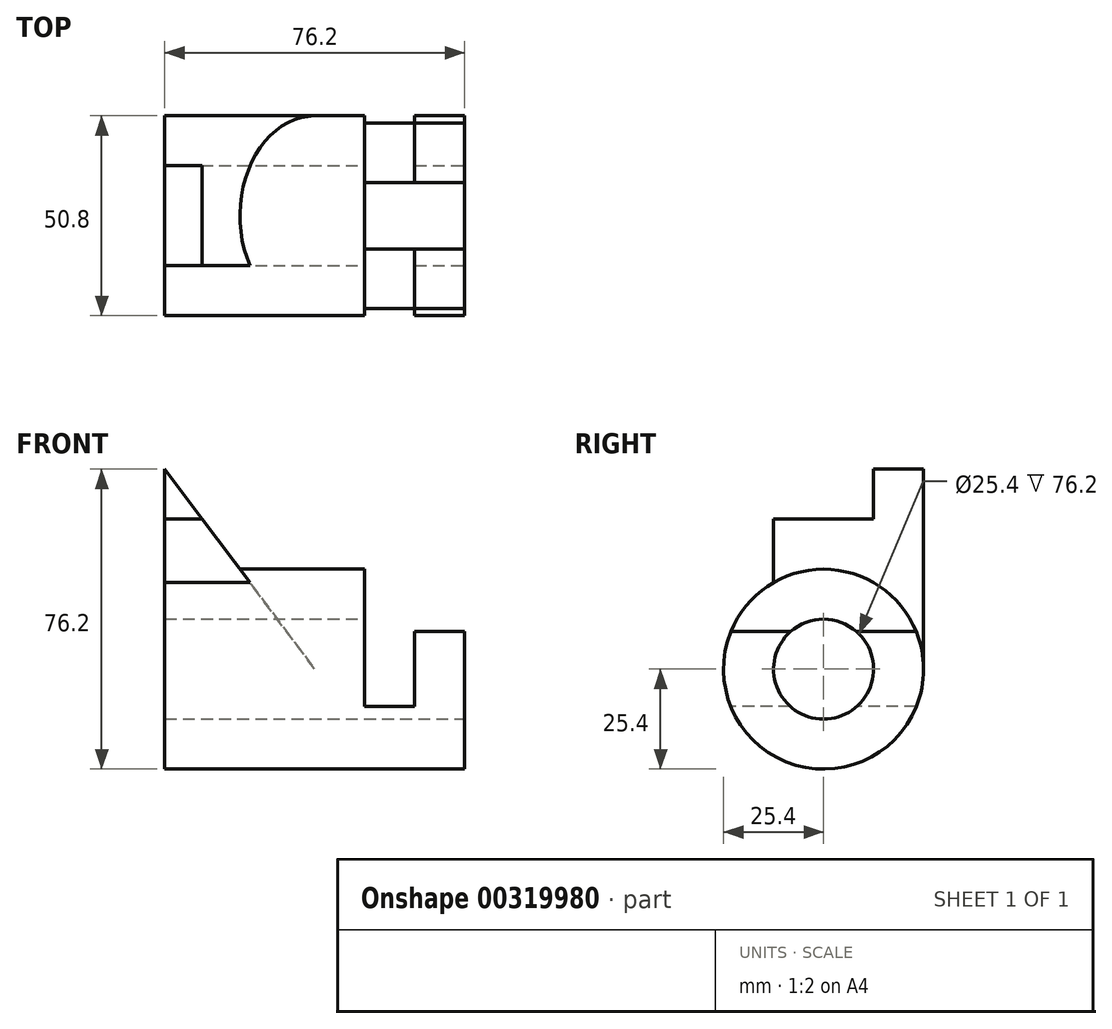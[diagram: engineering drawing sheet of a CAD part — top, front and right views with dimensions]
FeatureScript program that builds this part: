
annotation { "Feature Type Name" : "Feature", "Feature Type Description" : "" }
export const myFeature = defineFeature(function(context is Context, id is Id, definition is map)
    precondition{}
    {
        {
            var Q0;
            Q0=qCreatedBy(makeId("Right.planeOp"),FACE);
            var sketch = newSketch(context, id + "F0", { "sketchPlane" : qUnion([Q0])});
            skCircle(sketch, "E0", {"center": v(0, 0) * mm, "radius": 12.7 * mm});
            skCircle(sketch, "E1", {"center": v(0, 0) * mm, "radius": 25.4 * mm});
            skLineSegment(sketch, "E2", {"start": v(25.4, 0) * mm, "end": v(25.4, 50.8) * mm});
            skLineSegment(sketch, "E3", {"start": v(25.4, 50.8) * mm, "end": v(12.7, 50.8) * mm});
            skLineSegment(sketch, "E4", {"start": v(12.7, 50.8) * mm, "end": v(12.7, 38.1) * mm});
            skLineSegment(sketch, "E5", {"start": v(12.7, 38.1) * mm, "end": v(-12.7, 38.1) * mm});
            skLineSegment(sketch, "E6", {"start": v(-12.7, 38.1) * mm, "end": v(-12.7, 22) * mm});
            skSolve(sketch);
        }
        {
            var Q0;
            Q0 = qSketchRegion(id + "F0", true);
            extrude(context, id + "F1", {"entities" : qUnion([Q0]), "oppositeDirection" : true, "depth" : 76.2 * mm});
        }
        {
            var Q0;
            Q0=makeQuery(id+"F1.opExtrude","CAP_FACE",FACE,{"disambiguationData":[OSD([sQuery(id+"F0.wireOp",EDGE,"E0"),sQuery(id+"F0.wireOp",EDGE,"E1"),sQuery(id+"F0.wireOp",EDGE,"E2"),sQuery(id+"F0.wireOp",EDGE,"E3"),sQuery(id+"F0.wireOp",EDGE,"E4"),sQuery(id+"F0.wireOp",EDGE,"E5"),sQuery(id+"F0.wireOp",EDGE,"E6")])],"isStart":true});
            var sketch = newSketch(context, id + "F2", { "sketchPlane" : qUnion([Q0])});
            skLineSegment(sketch, "E7", {"start": v(25.4, 50.8) * mm, "end": v(-28.4, 50.8) * mm});
            skLineSegment(sketch, "E8", {"start": v(-28.4, 50.8) * mm, "end": v(-28.4, 9.52) * mm});
            skLineSegment(sketch, "E9", {"start": v(-28.4, 9.52) * mm, "end": v(25.4, 9.52) * mm});
            skLineSegment(sketch, "E10", {"start": v(25.4, 9.52) * mm, "end": v(25.4, 50.8) * mm});
            skSolve(sketch);
        }
        {
            var Q0;
            Q0 = qSketchRegion(id + "F2", true);
            extrude(context, id + "F3", {"entities" : qUnion([Q0]), "operationType" : NewBodyOperationType.REMOVE, "oppositeDirection" : true, "depth" : 25.4 * mm});
        }
        {
            var Q0;
            Q0=qCreatedBy(makeId("Front.planeOp"),FACE);
            var sketch = newSketch(context, id + "F4", { "sketchPlane" : qUnion([Q0])});
            skLineSegment(sketch, "E11.bottom", {"start": v(-25.4, 50.8) * mm, "end": v(-12.7, 50.8) * mm});
            skLineSegment(sketch, "E11.top", {"start": v(-25.4, -9.52) * mm, "end": v(-12.7, -9.52) * mm});
            skLineSegment(sketch, "E11.left", {"start": v(-25.4, 50.8) * mm, "end": v(-25.4, -9.52) * mm});
            skLineSegment(sketch, "E11.right", {"start": v(-12.7, 50.8) * mm, "end": v(-12.7, -9.52) * mm});
            skSolve(sketch);
        }
        {
            var Q0;
            Q0 = qSketchRegion(id + "F4", true);
            extrude(context, id + "F5", {"entities" : qUnion([Q0]), "operationType" : NewBodyOperationType.REMOVE, "endBound" : BoundingType.SYMMETRIC, "oppositeDirection" : true, "depth" : 254 * mm});
        }
        {
            var Q0;
            Q0=qCreatedBy(makeId("Front.planeOp"),FACE);
            var sketch = newSketch(context, id + "F6", { "sketchPlane" : qUnion([Q0])});
            skLineSegment(sketch, "E12", {"start": v(-76.2, 50.8) * mm, "end": v(-38.1, 0) * mm});
            skLineSegment(sketch, "E13", {"start": v(-38.1, 0) * mm, "end": v(-76.2, 0) * mm});
            skLineSegment(sketch, "E14", {"start": v(-76.2, 0) * mm, "end": v(-76.2, 50.8) * mm});
            skLineSegment(sketch, "E15", {"start": v(-76.2, 50.8) * mm, "end": v(-38.1, 50.8) * mm});
            skLineSegment(sketch, "E16", {"start": v(-38.1, 50.8) * mm, "end": v(-38.1, 0) * mm});
            skSolve(sketch);
        }
        {
            var Q0;
            Q0=makeQuery(id+"F6.imprint","IMPRINT",FACE,{"disambiguationData":[TD([[makeQuery(id+"F6.imprint","IMPRINT",EDGE,{"derivedFrom":sQuery(id+"F6.wireOp",EDGE,"E12")}),1.0]])]});
            extrude(context, id + "F7", {"entities" : qUnion([Q0]), "operationType" : NewBodyOperationType.REMOVE, "endBound" : BoundingType.THROUGH_ALL, "oppositeDirection" : true, "depth" : 25.4 * mm});
        }
        {
            var Q0;
            Q0=qCreatedBy(makeId("Front.planeOp"),FACE);
            var sketch = newSketch(context, id + "F8", { "sketchPlane" : qUnion([Q0])});
            skLineSegment(sketch, "E17.bottom", {"start": v(-38.1, 50.8) * mm, "end": v(-25.4, 50.8) * mm});
            skLineSegment(sketch, "E17.top", {"start": v(-38.1, 22) * mm, "end": v(-25.4, 22) * mm});
            skLineSegment(sketch, "E17.left", {"start": v(-38.1, 50.8) * mm, "end": v(-38.1, 22) * mm});
            skLineSegment(sketch, "E17.right", {"start": v(-25.4, 50.8) * mm, "end": v(-25.4, 22) * mm});
            skSolve(sketch);
        }
        {
            var Q0;
            Q0 = qSketchRegion(id + "F8", true);
            extrude(context, id + "F9", {"entities" : qUnion([Q0]), "operationType" : NewBodyOperationType.REMOVE, "endBound" : BoundingType.SYMMETRIC, "oppositeDirection" : true, "depth" : 254 * mm});
        }
        {
            var Q0;
            Q0=makeQuery(id+"F7.boolean.opBoolean","COPY",FACE,{"derivedFrom":makeQuery(id+"F7.opExtrude","SWEPT_FACE",FACE,{"disambiguationData":[OSD([sQuery(id+"F6.wireOp",EDGE,"E16")])]})});
            extrude(context, id + "F10", {"entities" : qUnion([Q0]), "operationType" : NewBodyOperationType.REMOVE, "oppositeDirection" : true, "depth" : 25.4 * mm});
        }
        {
            var Q0;
            {var subQ0=sQuery(id+"F6.wireOp",EDGE,"E16");Q0=makeQuery(id+"F10.boolean.opBoolean","MERGE",FACE,{"derivedFrom":[makeQuery(id+"F7.boolean.opBoolean","COPY",FACE,{"derivedFrom":makeQuery(id+"F7.opExtrude","CAP_FACE",FACE,{"disambiguationData":[OSD([sQuery(id+"F6.wireOp",EDGE,"E12"),sQuery(id+"F6.wireOp",EDGE,"E15"),subQ0])],"isStart":true})}),makeQuery(id+"F10.opExtrude","SWEPT_FACE",FACE,{"disambiguationData":[OSD([subQ0])]})]});}
            var sketch = newSketch(context, id + "F11", { "sketchPlane" : qUnion([Q0])});
            skLineSegment(sketch, "E18", {"start": v(38.1, 22) * mm, "end": v(54.6, 22) * mm});
            skLineSegment(sketch, "E19", {"start": v(54.6, 22) * mm, "end": v(66.67, 38.1) * mm});
            skLineSegment(sketch, "E20", {"start": v(66.67, 38.1) * mm, "end": v(38.1, 38.1) * mm});
            skLineSegment(sketch, "E21", {"start": v(38.1, 38.1) * mm, "end": v(38.1, 22) * mm});
            skSolve(sketch);
        }
        {
            var Q0;
            Q0 = qSketchRegion(id + "F11", true);
            extrude(context, id + "F12", {"entities" : qUnion([Q0]), "operationType" : NewBodyOperationType.REMOVE, "oppositeDirection" : true, "depth" : 25.4 * mm});
        }
        {
            var Q0;
            Q0=makeQuery(id+"F10.boolean.opBoolean","SPLIT",FACE,{"disambiguationData":[TD([makeQuery(id+"F5.boolean.opBoolean","COPY",FACE,{"disambiguationData":[OD(0.0)],"derivedFrom":makeQuery(id+"F5.opExtrude","SWEPT_FACE",FACE,{"disambiguationData":[OSD([sQuery(id+"F4.wireOp",EDGE,"E11.top")])]})})])],"derivedFrom":makeQuery(id+"F5.boolean.opBoolean","MERGE",FACE,{"derivedFrom":[makeQuery(id+"F3.boolean.opBoolean","COPY",FACE,{"derivedFrom":makeQuery(id+"F3.opExtrude","CAP_FACE",FACE,{"disambiguationData":[OSD([sQuery(id+"F2.wireOp",EDGE,"E7"),sQuery(id+"F2.wireOp",EDGE,"E8"),sQuery(id+"F2.wireOp",EDGE,"E9"),sQuery(id+"F2.wireOp",EDGE,"E10")])],"isStart":false})}),makeQuery(id+"F5.opExtrude","SWEPT_FACE",FACE,{"disambiguationData":[OSD([sQuery(id+"F4.wireOp",EDGE,"E11.left")])]})]})});
            var sketch = newSketch(context, id + "F13", { "sketchPlane" : qUnion([Q0])});
            skCircle(sketch, "E22", {"center": v(0, 0) * mm, "radius": 25.4 * mm});
            skCircle(sketch, "E23", {"center": v(0, 0) * mm, "radius": 12.7 * mm});
            skSolve(sketch);
        }
        {
            var Q0;
            Q0 = qSketchRegion(id + "F13", true);
            extrude(context, id + "F14", {"entities" : qUnion([Q0]), "operationType" : NewBodyOperationType.ADD, "oppositeDirection" : true, "depth" : 38.1 * mm});
        }
        {
            var Q0;
            Q0=makeQuery(id+"F1.opExtrude","CAP_FACE",FACE,{"disambiguationData":[OSD([sQuery(id+"F0.wireOp",EDGE,"E0"),sQuery(id+"F0.wireOp",EDGE,"E1"),sQuery(id+"F0.wireOp",EDGE,"E2"),sQuery(id+"F0.wireOp",EDGE,"E3"),sQuery(id+"F0.wireOp",EDGE,"E4"),sQuery(id+"F0.wireOp",EDGE,"E5"),sQuery(id+"F0.wireOp",EDGE,"E6")])],"isStart":true});
            var sketch = newSketch(context, id + "F15", { "sketchPlane" : qUnion([Q0])});
            skCircle(sketch, "E24", {"center": v(0, 0) * mm, "radius": 25.4 * mm});
            skLineSegment(sketch, "E25", {"start": v(23.55, 9.52) * mm, "end": v(25.4, 9.52) * mm});
            skLineSegment(sketch, "E26", {"start": v(25.4, 9.52) * mm, "end": v(25.4, 0) * mm});
            skSolve(sketch);
        }
        {
            var Q0;
            {var subQ2=sQuery(id+"F15.wireOp",EDGE,"E25");Q0=makeQuery(id+"F15.imprint","IMPRINT",FACE,{"disambiguationData":[TD([[makeQuery(id+"F15.imprint","IMPRINT",EDGE,{"derivedFrom":subQ2}),-1.0]])]});}
            extrude(context, id + "F16", {"entities" : qUnion([Q0]), "operationType" : NewBodyOperationType.REMOVE, "oppositeDirection" : true, "depth" : 25.4 * mm});
        }
    });
